# Revit family: МетеорЛифт_Лифт_Пассажирский_МетеорЛифт_EvoMRL_07-2023-1
name_source: partatom
category: Оборудование
units: mm (PartAtom-declared; Revit-internal decimal feet)

## family parameters
Всегда вертикально = Да
Общий = Да
При загрузке вырезать с полостями = Да
Размер круглого соединителя = Использовать диаметр
Тип детали = Нормальный
Точка расчета площади = Нет

## types (5) — shared parameters
Описание = Лифт электрический пассажирский без машинного помещения
Телефон = +7 (495) 974-24-40
zero-valued in all types: Отметка по умолчанию

## per-type parameters (varying)
| type | CD | CW | DL | NBPAS | URL | Изготовитель | Ось направляющих кабины | Ось подвески | Ось противовеса | Тип кабины | Штихмасс кабины | Элементы 13D | Элементы exc_13D |
| Г/п 450 кг / Кабина 1000х1250 мм (ШхГ) | 1250 мм | 1000 мм | 450 | 6 | https://meteor.ru | ООО "Метеор Лифт" | 420 мм | 625 мм | 727 мм | 06D | 1080 мм | Нет | Да |
| Г/п 630 кг / Кабина 1100х1400 (ШхГ) | 1400 мм | 1100 мм | 630 | 8 | https://www.otis.com | ООО "ОТИС Лифт" | 495 мм | 700 мм | 777 мм | 08D | 1180 мм | Нет | Да |
| Г/п 1000 кг / Кабина 1100х2100 (ШхГ) | 2100 мм | 1100 мм | 1000 | 13 | https://www.otis.com | ООО "ОТИС Лифт" | 1175 мм | 970 мм | 776 мм | 13D | 1190 мм | Да | Нет |
| Г/п 1000 кг / Кабина 1600х1400 (ШхГ) | 1400 мм | 1600 мм | 1000 | 13 | https://www.otis.com | ООО "ОТИС Лифт" | 495 мм | 700 мм | 1026 мм | 13W | 1690 мм | Нет | Да |
| Г/п 1000 кг / Кабина 2100х1100 (ШхГ) | 1100 мм | 2100 мм | 1000 | 13 | https://www.otis.com | ООО "ОТИС Лифт" | 345 мм | 550 мм | 1276 мм | 13X | 2190 мм | Нет | Да |

## geometry (parser evidence)
native form markers: Blend x4, Sweep x1
no freeform markers — native parametric forms only
